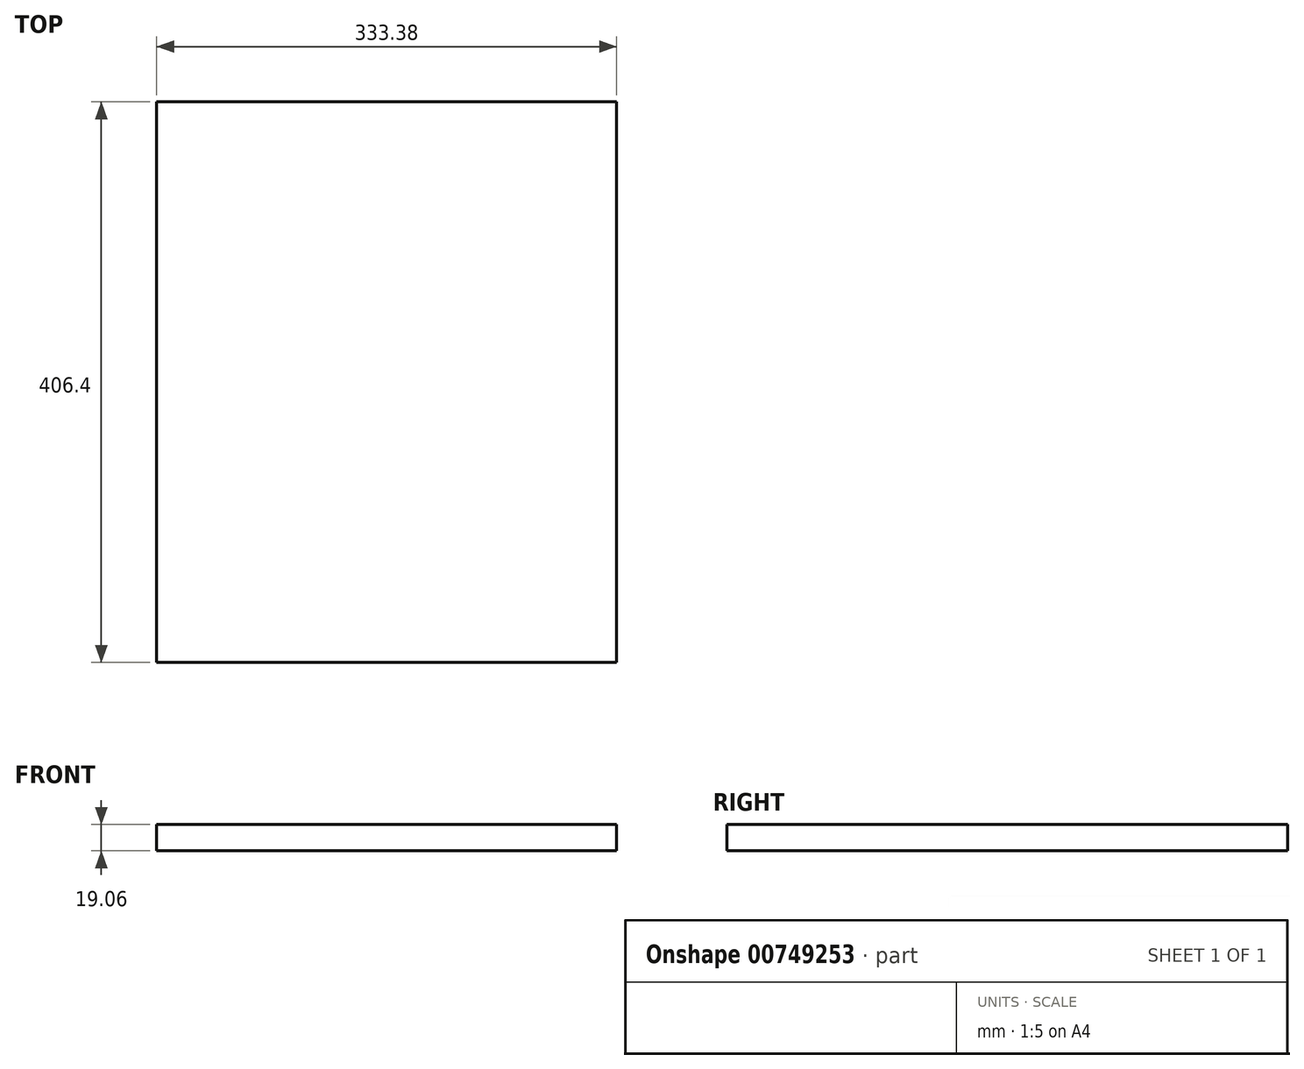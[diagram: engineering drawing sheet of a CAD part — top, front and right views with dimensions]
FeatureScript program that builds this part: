
annotation { "Feature Type Name" : "Feature", "Feature Type Description" : "" }
export const myFeature = defineFeature(function(context is Context, id is Id, definition is map)
    precondition{}
    {
        {
            var Q0;
            Q0=qCreatedBy(makeId("Right.planeOp"),FACE);
            var sketch = newSketch(context, id + "F0", { "sketchPlane" : qUnion([Q0])});
            skLineSegment(sketch, "E0.bottom", {"start": v(203.2, 9.53) * mm, "end": v(-203.2, 9.53) * mm});
            skLineSegment(sketch, "E0.top", {"start": v(203.2, -9.53) * mm, "end": v(-203.2, -9.53) * mm});
            skLineSegment(sketch, "E0.left", {"start": v(203.2, 9.53) * mm, "end": v(203.2, -9.52) * mm});
            skLineSegment(sketch, "E0.right", {"start": v(-203.2, 9.53) * mm, "end": v(-203.2, -9.52) * mm});
            skPoint(sketch, "E0.middle", {"position": v(0, 0) * mm});
            skSolve(sketch);
        }
        {
            var Q0;
            Q0=qSketchRegion(id+"F0",true);
            extrude(context, id + "F1", {"entities" : qUnion([Q0]), "depth" : 333.38 * mm, "offsetDistance" : 25.4 * mm});
        }
    });
